# Revit family: Hager-Volta-IP30-Flush_mounted-vide-NoHosted-CH-fr
name_source: partatom
category: Electrical Equipment
units: mm (PartAtom-declared; Revit-internal decimal feet)

## family parameters
Always vertical = Yes
Cut with Voids When Loaded = No
Panel Configuration = Two Columns, Circuits Across
Part Type = Panelboard
Room Calculation Point = No
Round Connector Dimension = Use Diameter
Shared = No
Work Plane-Based = Yes

## types (5) — shared parameters
Default Elevation = 1219 mm
EF000003 - mode de pose = EV000383 - encastré
EF000007 - couleur = EV000270 - gris
EF000049 - profondeur = 94 mm  [stored 0.308399 ft]
EF000116 - numéro RAL = 7035
EF000118 - avec cadre/support de montage = No
EF000218 - profondeur d'encastrement = 90 mm  [stored 0.295276 ft]
EF000846 - largeur d'encastrement = 335 mm  [stored 1.09908 ft]
EF001062 - finition CEM = Yes
EF001088 - possibilité de montage en saillie = Yes
EF001131 - profondeur intérieure = 92 mm
EF001134 - rail DIN = No
EF001596 - matériau du boîtier/corps = EV000139 - plastique
EF002950 - largeur en nombre de modules = 12
EF006244 - couvercle/porte transparent(e) = No
EF006306 - avec serrure = No
EF009212 - finition du couvercle = EV000116 - fermé
EF015776 - borne de mise à la terre = No
EF015777 - borne à conducteur neutre = No
EF015941 - porte pour transmission du signal = No
HG000002 - avec porte = No
HG000003 - Gamme = Volta
HG000005 - Epaisseur = 3 mm  [stored 0.00984252 ft]
HG000006 - Encastré = Yes
HG000009 - Porte à double battant = No
HG000010 - Portes asymétriques = No
HG000011 - Rangées du bas vides = No
HG000017 - Distance entre pôles = 18 mm  [stored 0.0590551 ft]
Manufacturer = Hager
Type Comments = Volta
zero-valued in all types: HG000001 - nombre de colonnes, HG000007 - Nombre de colonnes vides, HG000008 - Nombre de rangées vides

## per-type parameters (varying)
| type | EF000008 - largeur | EF000040 - hauteur | EF000266 - nombre de rangées | EF000332 - hauteur d'encastrement | HG000004 - Référence fabricant | Model |
| Encastré  L330 H355 P94.5 12 Modules - VU12NK | 330 mm | 355 mm | 1 | 346 mm | VU12NK | VU12NK |
| Encastré  L330 H484 P94.5 12 Modules - VU24NK | 330 mm | 484 mm | 2 | 471 mm | VU24NK | VU24NK |
| Encastré  L330 H609 P94.5 12 Modules - VU36NK | 330 mm | 609 mm | 3 | 596 mm | VU36NK | VU36NK |
| Encastré  L330 H734 P94.5 12 Modules - VU48NK | 330 mm | 734 mm | 4 | 721 mm | VU48NK | VU48NK |
| Encastré  L348 H880 P94.5 12 Modules - VU60NK | 348 mm  [stored 1.14173 ft] | 880 mm  [stored 2.88714 ft] | 5 | 846 mm  [stored 2.77559 ft] | VU60NK | VU60NK |

note: [stored X ft] marks values corroborated as IEEE doubles in the binary element streams (Revit-internal decimal feet)

## geometry (parser evidence)
native form markers: Sweep x13
no freeform markers — native parametric forms only
